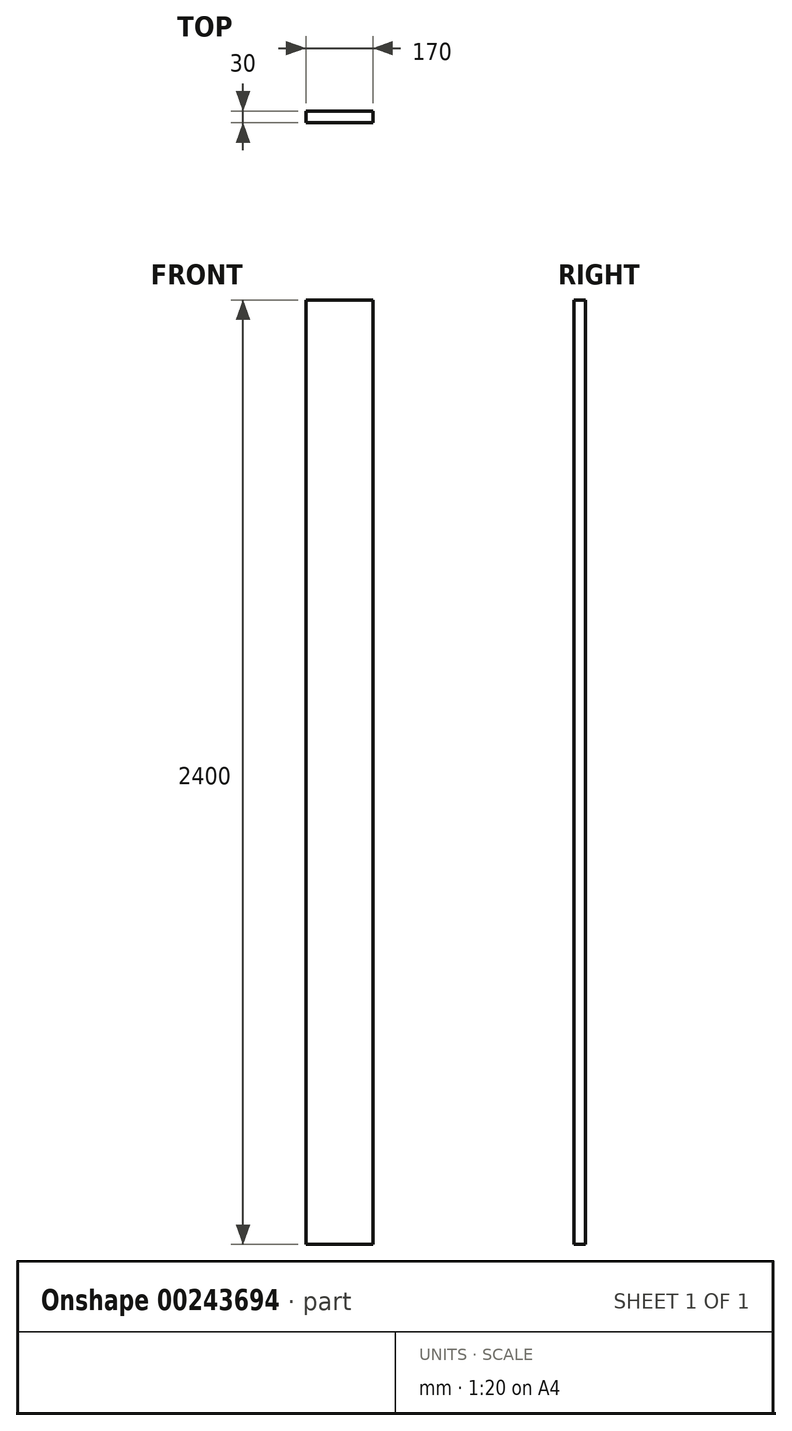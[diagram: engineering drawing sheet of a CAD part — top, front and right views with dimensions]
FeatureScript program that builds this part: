
annotation { "Feature Type Name" : "Feature", "Feature Type Description" : "" }
export const myFeature = defineFeature(function(context is Context, id is Id, definition is map)
    precondition{}
    {
        {
            var Q0;
            Q0=qCreatedBy(makeId("Front.planeOp"),FACE);
            var sketch = newSketch(context, id + "F0", { "sketchPlane" : qUnion([Q0])});
            skLineSegment(sketch, "E0.bottom", {"start": v(-85, 1200) * mm, "end": v(85, 1200) * mm});
            skLineSegment(sketch, "E0.top", {"start": v(-85, -1200) * mm, "end": v(85, -1200) * mm});
            skLineSegment(sketch, "E0.left", {"start": v(-85, 1200) * mm, "end": v(-85, -1200) * mm});
            skLineSegment(sketch, "E0.right", {"start": v(85, 1200) * mm, "end": v(85, -1200) * mm});
            skLineSegment(sketch, "E1", {"start": v(0, 1200) * mm, "end": v(0, -1200) * mm, "construction": true});
            skLineSegment(sketch, "E2", {"start": v(-85, 0) * mm, "end": v(85, 0) * mm, "construction": true});
            skSolve(sketch);
        }
        {
            var Q0;
            Q0=makeQuery(id+"F0.imprint","IMPRINT",FACE,{"disambiguationData":[TD([[makeQuery(id+"F0.imprint","IMPRINT",EDGE,{"derivedFrom":sQuery(id+"F0.wireOp",EDGE,"E0.bottom")}),-1.0]])]});
            extrude(context, id + "F1", {"entities" : qUnion([Q0]), "endBound" : BoundingType.SYMMETRIC, "depth" : 30 * mm});
        }
    });
